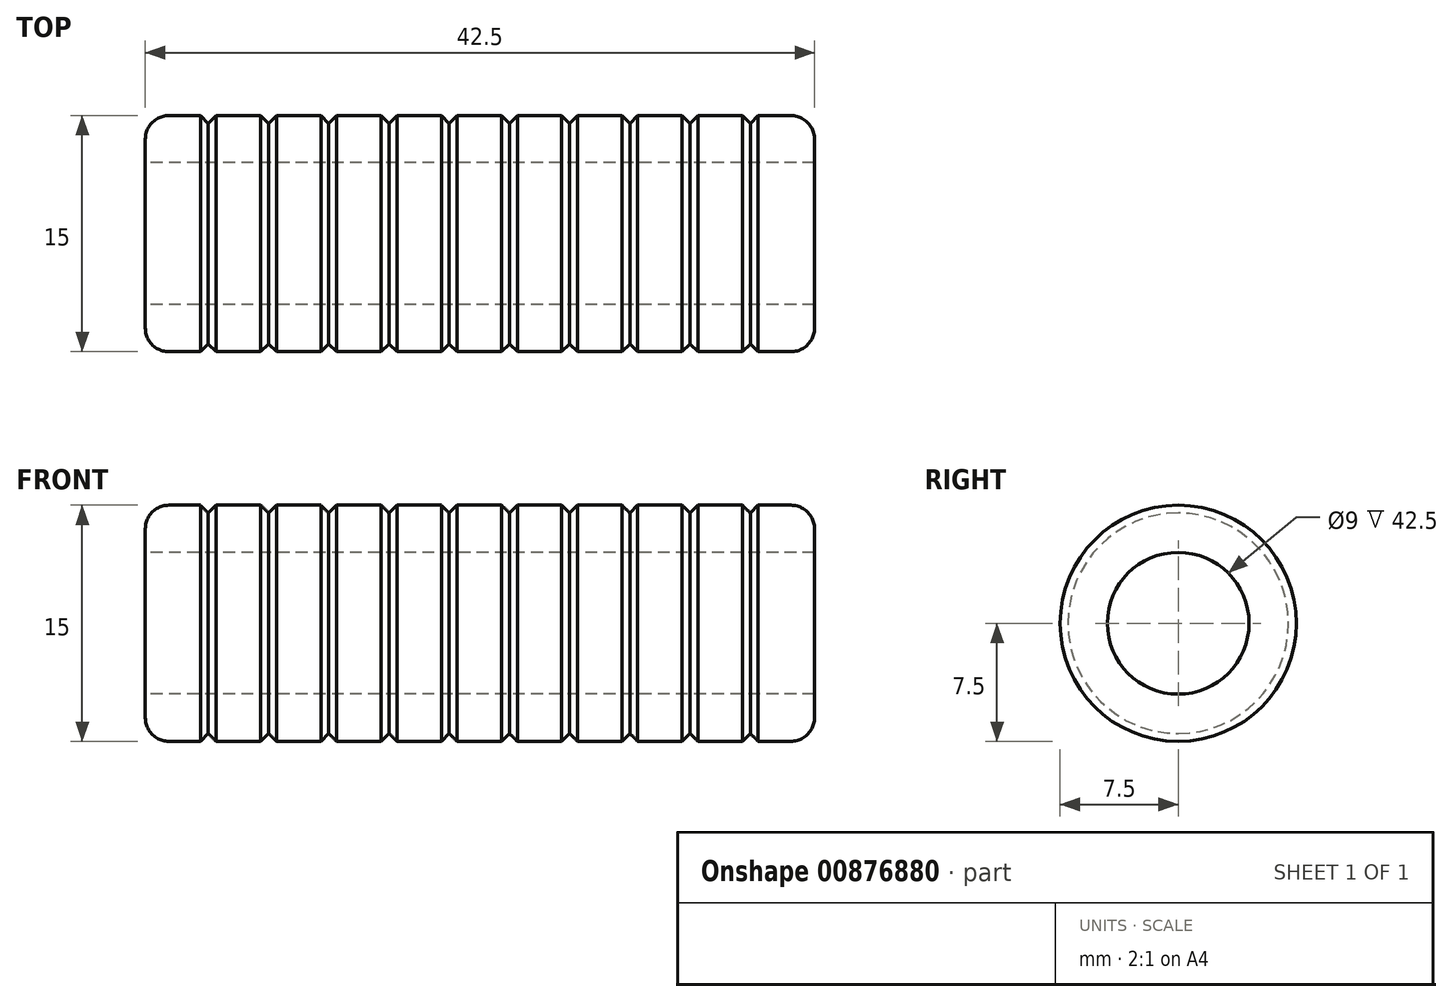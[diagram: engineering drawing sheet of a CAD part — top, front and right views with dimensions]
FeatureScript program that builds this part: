
annotation { "Feature Type Name" : "Feature", "Feature Type Description" : "" }
export const myFeature = defineFeature(function(context is Context, id is Id, definition is map)
    precondition{}
    {
        {
            var Q0;
            Q0=qCreatedBy(makeId("Right.planeOp"),FACE);
            var sketch = newSketch(context, id + "F0", { "sketchPlane" : qUnion([Q0])});
            skCircle(sketch, "E0", {"center": v(0, 0) * mm, "radius": 7.5 * mm});
            skCircle(sketch, "E1", {"center": v(0, 0) * mm, "radius": 4.5 * mm});
            skSolve(sketch);
        }
        {
            var Q0;
            Q0=makeQuery(id+"F0.imprint","IMPRINT",FACE,{"disambiguationData":[TD([[makeQuery(id+"F0.imprint","IMPRINT",EDGE,{"derivedFrom":sQuery(id+"F0.wireOp",EDGE,"E0")}),1.0]])]});
            extrude(context, id + "F1", {"entities" : qUnion([Q0]), "depth" : 42.5 * mm, "offsetDistance" : 25 * mm});
        }
        {
            var Q0;
            Q0=makeQuery(id+"F1.opExtrude","CAP_EDGE",EDGE,{"disambiguationData":[OSD([sQuery(id+"F0.wireOp",EDGE,"E0")])],"isStart":false});
            var Q1;
            Q1=makeQuery(id+"F1.opExtrude","CAP_EDGE",EDGE,{"disambiguationData":[OSD([sQuery(id+"F0.wireOp",EDGE,"E0")])],"isStart":true});
            fillet(context, id + "F2", {"entities" : qUnion([Q0, Q1]), "radius" : 1.5 * mm, "tangentPropagation" : true, "allowEdgeOverflow" : false});
        }
        {
            var Q0;
            Q0=qCreatedBy(makeId("Right.planeOp"),FACE);
            cPlane(context, id + "F3", {"entities" : qUnion([Q0]), "cplaneType" : CPlaneType.OFFSET, "offset" : 5 * mm, "width" : 150 * mm, "height" : 150 * mm});
        }
        {
            var Q0;
            Q0=qCreatedBy(id+"F3.planeOp",FACE);
            var sketch = newSketch(context, id + "F4", { "sketchPlane" : qUnion([Q0])});
            skCircle(sketch, "E2", {"center": v(0, 9) * mm, "radius": 1.75 * mm});
            skSolve(sketch);
        }
        {
            var Q0;
            Q0=qCreatedBy(makeId("Front.planeOp"),FACE);
            var sketch = newSketch(context, id + "F5", { "sketchPlane" : qUnion([Q0])});
            skLineSegment(sketch, "E3", {"start": v(0, 0) * mm, "end": v(42.5, 0) * mm});
            skSolve(sketch);
        }
        {
            var Q0;
            Q0=qCreatedBy(makeId("Front.planeOp"),FACE);
            var sketch = newSketch(context, id + "F6", { "sketchPlane" : qUnion([Q0])});
            skLineSegment(sketch, "E4", {"start": v(2.59, 8.41) * mm, "end": v(4, 7) * mm});
            skLineSegment(sketch, "E5", {"start": v(4, 7) * mm, "end": v(5.41, 8.41) * mm});
            skLineSegment(sketch, "E6", {"start": v(4, 7) * mm, "end": v(38.5, 7) * mm});
            skLineSegment(sketch, "E7", {"start": v(2.59, 8.41) * mm, "end": v(5.41, 8.41) * mm});
            skLineSegment(sketch, "E8.1.0.0", {"start": v(7.82, 7) * mm, "end": v(9.24, 8.41) * mm});
            skLineSegment(sketch, "E8.1.0.1", {"start": v(6.41, 8.41) * mm, "end": v(9.24, 8.41) * mm});
            skLineSegment(sketch, "E8.1.0.2", {"start": v(6.41, 8.41) * mm, "end": v(7.83, 7) * mm});
            skLineSegment(sketch, "E8.2.0.0", {"start": v(11.65, 7) * mm, "end": v(13.06, 8.41) * mm});
            skLineSegment(sketch, "E8.2.0.1", {"start": v(10.24, 8.41) * mm, "end": v(13.06, 8.41) * mm});
            skLineSegment(sketch, "E8.2.0.2", {"start": v(10.24, 8.41) * mm, "end": v(11.65, 7) * mm});
            skLineSegment(sketch, "E8.3.0.0", {"start": v(15.47, 7) * mm, "end": v(16.89, 8.41) * mm});
            skLineSegment(sketch, "E8.3.0.1", {"start": v(14.06, 8.41) * mm, "end": v(16.89, 8.41) * mm});
            skLineSegment(sketch, "E8.3.0.2", {"start": v(14.06, 8.41) * mm, "end": v(15.48, 7) * mm});
            skLineSegment(sketch, "E8.4.0.0", {"start": v(19.3, 7) * mm, "end": v(20.71, 8.41) * mm});
            skLineSegment(sketch, "E8.4.0.1", {"start": v(17.89, 8.41) * mm, "end": v(20.71, 8.41) * mm});
            skLineSegment(sketch, "E8.4.0.2", {"start": v(17.89, 8.41) * mm, "end": v(19.3, 7) * mm});
            skLineSegment(sketch, "E8.5.0.0", {"start": v(23.12, 7) * mm, "end": v(24.54, 8.41) * mm});
            skLineSegment(sketch, "E8.5.0.1", {"start": v(21.71, 8.41) * mm, "end": v(24.54, 8.41) * mm});
            skLineSegment(sketch, "E8.5.0.2", {"start": v(21.71, 8.41) * mm, "end": v(23.12, 7) * mm});
            skLineSegment(sketch, "E8.6.0.0", {"start": v(26.95, 7) * mm, "end": v(28.36, 8.41) * mm});
            skLineSegment(sketch, "E8.6.0.1", {"start": v(25.54, 8.41) * mm, "end": v(28.36, 8.41) * mm});
            skLineSegment(sketch, "E8.6.0.2", {"start": v(25.54, 8.41) * mm, "end": v(26.95, 7) * mm});
            skLineSegment(sketch, "E8.7.0.0", {"start": v(30.77, 7) * mm, "end": v(32.19, 8.41) * mm});
            skLineSegment(sketch, "E8.7.0.1", {"start": v(29.36, 8.41) * mm, "end": v(32.19, 8.41) * mm});
            skLineSegment(sketch, "E8.7.0.2", {"start": v(29.36, 8.41) * mm, "end": v(30.78, 7) * mm});
            skLineSegment(sketch, "E8.8.0.0", {"start": v(34.6, 7) * mm, "end": v(36.01, 8.41) * mm});
            skLineSegment(sketch, "E8.8.0.1", {"start": v(33.19, 8.41) * mm, "end": v(36.01, 8.41) * mm});
            skLineSegment(sketch, "E8.8.0.2", {"start": v(33.19, 8.41) * mm, "end": v(34.6, 7) * mm});
            skLineSegment(sketch, "E8.9.0.0", {"start": v(38.42, 7) * mm, "end": v(39.84, 8.41) * mm});
            skLineSegment(sketch, "E8.9.0.1", {"start": v(37.01, 8.41) * mm, "end": v(39.84, 8.41) * mm});
            skLineSegment(sketch, "E8.9.0.2", {"start": v(37.01, 8.41) * mm, "end": v(38.43, 7) * mm});
            skLineSegment(sketch, "E8.direction1", {"start": v(4, 7) * mm, "end": v(7.83, 7) * mm, "construction": true});
            skSolve(sketch);
        }
        {
            var Q0;
            Q0 = qSketchRegion(id + "F6", true);
            var Q1;
            Q1=sQuery(id+"F5.wireOp",EDGE,"E3");
            revolve(context, id + "F7", {"operationType" : NewBodyOperationType.REMOVE, "surfaceOperationType" : NewSurfaceOperationType.NEW, "entities" : qUnion([Q0]), "axis" : qUnion([Q1]), "revolveType" : RevolveType.FULL, "oppositeDirection" : true});
        }
    });
